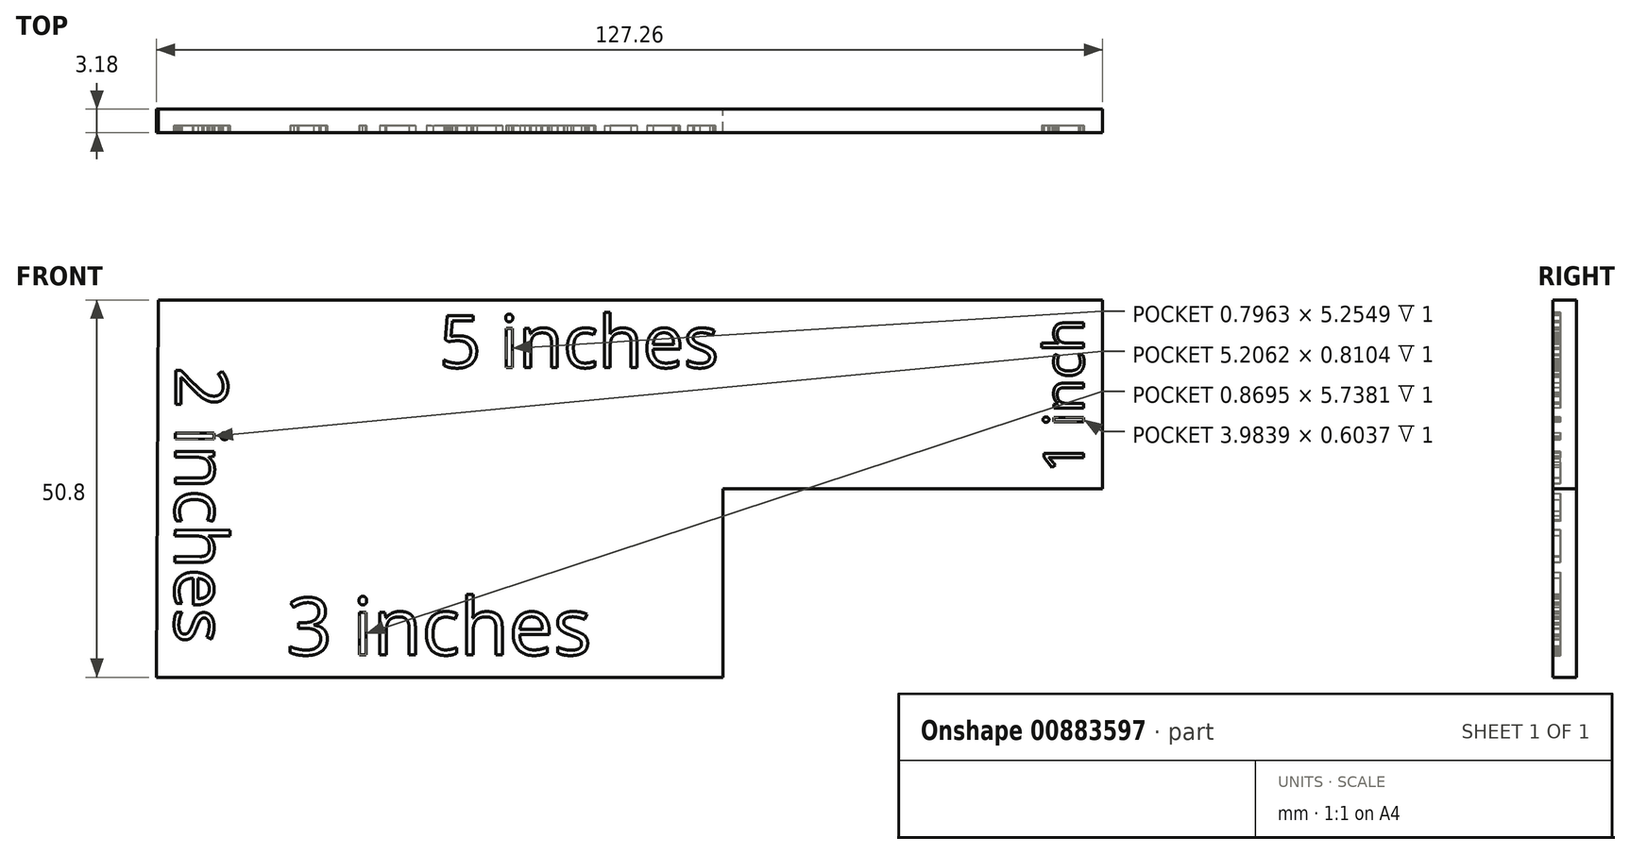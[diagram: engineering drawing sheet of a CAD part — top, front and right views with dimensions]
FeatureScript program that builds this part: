
annotation { "Feature Type Name" : "Feature", "Feature Type Description" : "" }
export const myFeature = defineFeature(function(context is Context, id is Id, definition is map)
    precondition{}
    {
        {
            var Q0;
            Q0=qCreatedBy(makeId("Front.planeOp"),FACE);
            var sketch = newSketch(context, id + "F0", { "sketchPlane" : qUnion([Q0])});
            skLineSegment(sketch, "E0", {"start": v(-43.76, 0) * mm, "end": v(83.24, 0) * mm});
            skLineSegment(sketch, "E1", {"start": v(83.24, 0) * mm, "end": v(83.24, -25.4) * mm});
            skLineSegment(sketch, "E2", {"start": v(83.24, -25.4) * mm, "end": v(32.18, -25.4) * mm});
            skLineSegment(sketch, "E3", {"start": v(32.18, -25.4) * mm, "end": v(32.18, -50.8) * mm});
            skLineSegment(sketch, "E4", {"start": v(32.18, -50.8) * mm, "end": v(-44.02, -50.8) * mm});
            skLineSegment(sketch, "E5", {"start": v(-44.02, -50.8) * mm, "end": v(-43.76, 0) * mm});
            skSolve(sketch);
        }
        {
            var Q0;
            Q0=makeQuery(id+"F0.imprint","IMPRINT",FACE,{"disambiguationData":[TD([[makeQuery(id+"F0.imprint","IMPRINT",EDGE,{"derivedFrom":sQuery(id+"F0.wireOp",EDGE,"E0")}),-1.0]])]});
            extrude(context, id + "F1", {"entities" : qUnion([Q0]), "depth" : 3.17 * mm, "offsetDistance" : 25.4 * mm});
        }
        {
            var Q0;
            Q0=makeQuery(id+"F1.opExtrude","CAP_FACE",FACE,{"disambiguationData":[OSD([sQuery(id+"F0.wireOp",EDGE,"E0"),sQuery(id+"F0.wireOp",EDGE,"E1"),sQuery(id+"F0.wireOp",EDGE,"E2"),sQuery(id+"F0.wireOp",EDGE,"E3"),sQuery(id+"F0.wireOp",EDGE,"E4"),sQuery(id+"F0.wireOp",EDGE,"E5")])],"isStart":false});
            var sketch = newSketch(context, id + "F2", { "sketchPlane" : qUnion([Q0])});
            skText(sketch, "E6", { "text": "5 inches", "fontName": "OpenSans-Regular.ttf"});
            const initialGuessF2  = {"E6": [-0.00598, -0.0091, 1, 0, 0.00707]};
            skSetInitialGuess(sketch, initialGuessF2);
            skSolve(sketch);
        }
        {
            var Q0;
            Q0 = qSketchRegion(id + "F2", true);
            extrude(context, id + "F3", {"entities" : qUnion([Q0]), "operationType" : NewBodyOperationType.REMOVE, "oppositeDirection" : true, "depth" : 1 * mm, "offsetDistance" : 25.4 * mm});
        }
        {
            var Q0;
            {var subQ0=sQuery(id+"F0.wireOp",EDGE,"E1");var subQ1=sQuery(id+"F0.wireOp",EDGE,"E3");var subQ2=sQuery(id+"F0.wireOp",EDGE,"E0");var subQ3=sQuery(id+"F0.wireOp",EDGE,"E4");var subQ4=sQuery(id+"F0.wireOp",EDGE,"E5");var subQ5=sQuery(id+"F0.wireOp",EDGE,"E2");Q0=makeQuery(id+"F3.boolean.opBoolean","SPLIT",FACE,{"disambiguationData":[TD([makeQuery(id+"F1.opExtrude","SWEPT_FACE",FACE,{"disambiguationData":[OSD([subQ2])]})])],"derivedFrom":makeQuery(id+"F1.opExtrude","CAP_FACE",FACE,{"disambiguationData":[OSD([subQ2,subQ0,subQ5,subQ1,subQ3,subQ4])],"isStart":false})});}
            var sketch = newSketch(context, id + "F4", { "sketchPlane" : qUnion([Q0])});
            skText(sketch, "E7", { "text": "2 inches", "fontName": "OpenSans-Regular.ttf"});
            const initialGuessF4  = {"E7": [-0.04142, -0.00899, -0.00423, -1, 0.007]};
            skSetInitialGuess(sketch, initialGuessF4);
            skSolve(sketch);
        }
        {
            var Q0;
            Q0 = qSketchRegion(id + "F4", true);
            extrude(context, id + "F5", {"entities" : qUnion([Q0]), "operationType" : NewBodyOperationType.REMOVE, "oppositeDirection" : true, "depth" : 1 * mm, "offsetDistance" : 25.4 * mm});
        }
        {
            var Q0;
            {var subQ6=sQuery(id+"F0.wireOp",EDGE,"E2");var subQ73=sQuery(id+"F0.wireOp",EDGE,"E5");var subQ80=sQuery(id+"F0.wireOp",EDGE,"E0");var subQ81=makeQuery(id+"F1.opExtrude","SWEPT_FACE",FACE,{"disambiguationData":[OSD([subQ80])]});var subQ86=sQuery(id+"F0.wireOp",EDGE,"E4");var subQ91=sQuery(id+"F0.wireOp",EDGE,"E3");var subQ95=sQuery(id+"F0.wireOp",EDGE,"E1");Q0=makeQuery(id+"F5.boolean.opBoolean","SPLIT",FACE,{"disambiguationData":[TD([subQ81])],"derivedFrom":makeQuery(id+"F3.boolean.opBoolean","SPLIT",FACE,{"disambiguationData":[TD([subQ81])],"derivedFrom":makeQuery(id+"F1.opExtrude","CAP_FACE",FACE,{"disambiguationData":[OSD([subQ80,subQ95,subQ6,subQ91,subQ86,subQ73])],"isStart":false})})});}
            var sketch = newSketch(context, id + "F6", { "sketchPlane" : qUnion([Q0])});
            skText(sketch, "E8", { "text": "3 inches", "fontName": "OpenSans-Regular.ttf"});
            skPoint(sketch, "E9", {"position": v(-5.92, -50.8) * mm});
            skText(sketch, "E10", { "text": "1 inch", "fontName": "OpenSans-Regular.ttf"});
            const initialGuessF6  = {"E8": [-0.02654, -0.04777, 1, 0, 0.00772], "E10": [0.08069, -0.02324, 0, 1, 0.00536]};
            skSetInitialGuess(sketch, initialGuessF6);
            skSolve(sketch);
        }
        {
            var Q0;
            Q0 = qSketchRegion(id + "F6", true);
            extrude(context, id + "F7", {"entities" : qUnion([Q0]), "operationType" : NewBodyOperationType.REMOVE, "oppositeDirection" : true, "depth" : mm, "offsetDistance" : 25.4 * mm});
        }
    });
